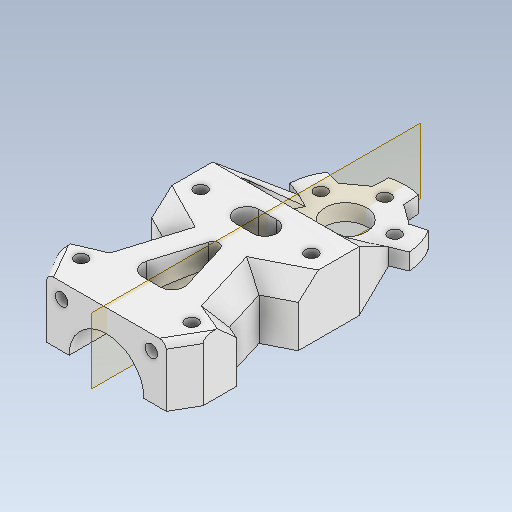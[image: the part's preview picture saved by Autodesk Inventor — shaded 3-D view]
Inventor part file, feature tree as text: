
AUTODESK INVENTOR PART (.ipt)
format: ipt  version: 2020 (Build 240168000, 168)  size: 375,296 bytes
history: native  units: mm
features: reference x14, sketch x9, extrude x6, projected_geometry x4, other x4, chamfer x3, plane x2, thicken_offset x2, mirror x2, fillet x2, loft x1, hole x1
ambient origin geometry x8: Origin, YZ Plane, XZ Plane, XY Plane, X Axis, Y Axis, Z Axis, Center Point
bodies: Solid1 (feature_tree)
feature tree (50):
  sketch  "Sketch1"  dims[d0=25.0mm d1=20.0mm]
  plane  "Work Plane1"
  extrude  "Extrusion1"  Depth=20.0mm
  extrude  "Extrusion2"  Depth=10.0mm TaperAngle=0.0deg
  extrude  "Extrusion3"  Depth=20.0mm TaperAngle=0.0deg
  thicken_offset  "Thicken1"
  thicken_offset  "Thicken2"
  extrude  "Extrusion4"  Depth=1.0mm
  loft  "Loft1"
  plane  "Work Plane2"
  mirror  "Mirror1"
  hole  "Hole1"  [1 undecoded]
  chamfer  "Chamfer2"  Angle=90.0deg  [1 undecoded]
  chamfer  "Chamfer3"  Angle=90.0deg  [1 undecoded]
  extrude  "Extrusion7"  Depth=3.0mm TaperAngle=60.0deg
  chamfer  "Chamfer4"  Distance=4.5mm Angle=60.0deg
  mirror  "Mirror3"
  fillet  "Fillet2"  Radius=20.0mm
  extrude  "Extrusion8"  Depth=3.0mm TaperAngle=60.0deg
  fillet  "Fillet3"  Radius=2.0mm
  reference  "Reference1"
  sketch  "Sketch2"  dims[d2=20.0mm d3=10.0mm d4=0.0mm]
  reference  "Reference2"
  reference  "Reference3"
  reference  "Reference4"
  reference  "Reference5"
  sketch  "Sketch3"  dims[d5=20.0mm d6=0.0mm d7=20.0mm d8=0.0mm]
  reference  "Reference6"
  sketch  "Sketch4"  dims[d9=1.0mm d10=1.0mm]
  reference  "Reference7"
  projected_geometry  "Projected Loop1"
  sketch  "Sketch6"  dims[d11=1.0mm d12=1.0mm]
  projected_geometry  "Projected Loop3"
  sketch  "Sketch7"  dims[d13=5.5mm d14=0.0mm d17=6.0mm]
  projected_geometry  "Projected Loop4"
  sketch  "Sketch9"  dims[d18=5.0mm]
  reference  "Reference13"
  reference  "Reference14"
  sketch  "Sketch10"  dims[d19=6.0mm d20=0.0mm d21=90.0deg d22=0.0mm d23=90.0deg]
  reference  "Reference15"
  reference  "Reference16"
  reference  "Reference17"
  reference  "Reference18"
  reference  "Reference19"
  sketch  "Sketch11"  dims[d29=4.2mm d30=5.98424mm d31=3.023mm d32=2.0mm d33=14.3117mm d34=5.0mm d35=0.0mm d36=4.5mm d37=2.0mm d38=60.0deg d39=4.5mm d40=2.0mm d41=60.0deg d43=20.0mm d44=0.0mm d45=6.0mm d46=2.0mm d47=60.0deg d48=2.0mm d49=3.0mm d50=8.0mm d51=20.0mm d52=0.0mm d53=3.0mm]
  projected_geometry  "Projected Loop6"
  parser-record x1  (decoder bookkeeping rows leaked as tree rows — omitted from the tree; the rows remain in map.json)
  other  "sub_leg_1.iam"
  other  "joint_connector_4:1"
  other  "joint_connector_6:1"
note: 3 required parameter values undecoded (feature->parameter linkage not recoverable at this tier; creation-order binding heuristic only, values carry confidence <= 0.55)
note: 1 file-system path scrubbed to <path> (originals preserved in map.json)
